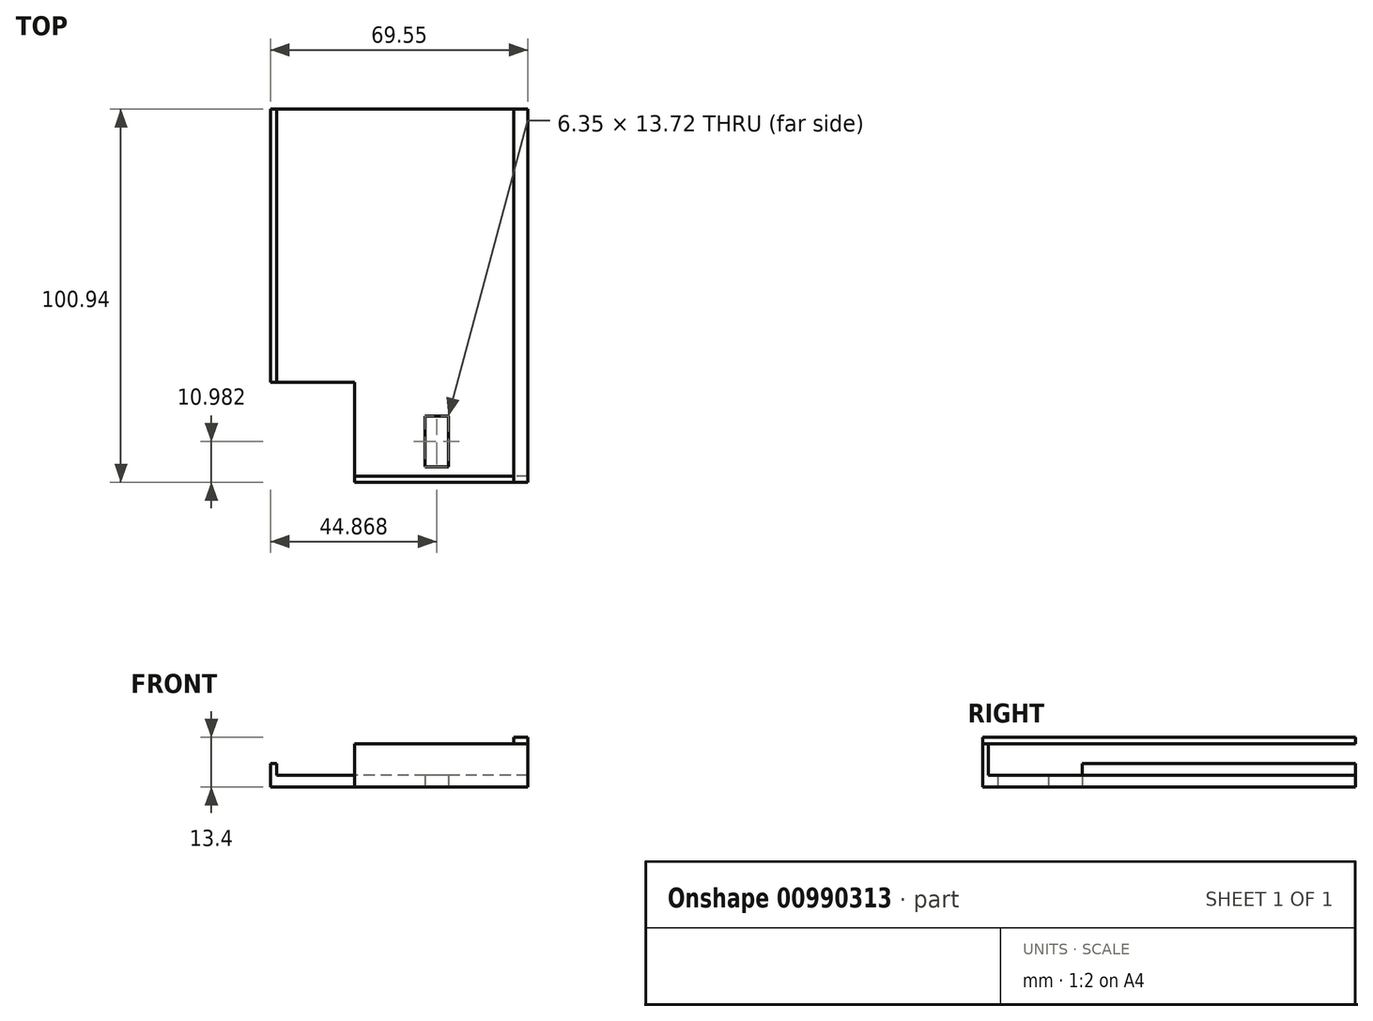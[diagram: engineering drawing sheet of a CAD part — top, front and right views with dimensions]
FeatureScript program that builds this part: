
annotation { "Feature Type Name" : "Feature", "Feature Type Description" : "" }
export const myFeature = defineFeature(function(context is Context, id is Id, definition is map)
    precondition{}
    {
        {
            var Q0;
            Q0=qCreatedBy(makeId("Top.planeOp"),FACE);
            var sketch = newSketch(context, id + "F0", { "sketchPlane" : qUnion([Q0])});
            skLineSegment(sketch, "E0.bottom", {"start": v(33.98, 49.68) * mm, "end": v(-33.98, 49.68) * mm});
            skLineSegment(sketch, "E0.top", {"start": v(33.98, -49.68) * mm, "end": v(-33.98, -49.68) * mm});
            skLineSegment(sketch, "E0.left", {"start": v(33.98, 49.68) * mm, "end": v(33.98, -49.68) * mm});
            skLineSegment(sketch, "E0.right", {"start": v(-33.98, 49.68) * mm, "end": v(-33.98, -49.68) * mm});
            skPoint(sketch, "E0.middle", {"position": v(0, 0) * mm});
            skLineSegment(sketch, "E1.bottom", {"start": v(33.98, 49.68) * mm, "end": v(33.98, 49.68) * mm});
            skLineSegment(sketch, "E1.top", {"start": v(33.98, -49.68) * mm, "end": v(33.98, -49.68) * mm});
            skLineSegment(sketch, "E2.top", {"start": v(-33.98, -24.28) * mm, "end": v(-12.93, -24.28) * mm});
            skLineSegment(sketch, "E2.right", {"start": v(-12.93, -49.68) * mm, "end": v(-12.93, -24.28) * mm});
            skLineSegment(sketch, "E3.bottom", {"start": v(-12.93, -49.68) * mm, "end": v(33.98, -49.68) * mm});
            skLineSegment(sketch, "E3.top", {"start": v(-12.93, -51.26) * mm, "end": v(33.98, -51.26) * mm});
            skLineSegment(sketch, "E3.left", {"start": v(-12.93, -49.68) * mm, "end": v(-12.93, -51.26) * mm});
            skLineSegment(sketch, "E3.right", {"start": v(33.98, -49.68) * mm, "end": v(33.98, -51.26) * mm});
            skLineSegment(sketch, "E4.bottom", {"start": v(-33.98, 49.68) * mm, "end": v(-35.57, 49.68) * mm});
            skLineSegment(sketch, "E4.top", {"start": v(-33.98, -49.68) * mm, "end": v(-35.57, -49.68) * mm});
            skLineSegment(sketch, "E4.right", {"start": v(-35.57, 49.68) * mm, "end": v(-35.57, -49.68) * mm});
            skLineSegment(sketch, "E5", {"start": v(-33.98, -43.18) * mm, "end": v(33.98, -43.18) * mm, "construction": true});
            skLineSegment(sketch, "E6", {"start": v(-33.98, -24.28) * mm, "end": v(-35.57, -24.28) * mm});
            skLineSegment(sketch, "E7.bottom", {"start": v(12.47, -47.14) * mm, "end": v(6.12, -47.14) * mm});
            skLineSegment(sketch, "E7.top", {"start": v(12.47, -33.42) * mm, "end": v(6.12, -33.42) * mm});
            skLineSegment(sketch, "E7.left", {"start": v(12.47, -47.14) * mm, "end": v(12.47, -33.42) * mm});
            skLineSegment(sketch, "E7.right", {"start": v(6.12, -47.14) * mm, "end": v(6.12, -33.42) * mm});
            skSolve(sketch);
        }
        {
            var Q0;
            {var subQ3=sQuery(id+"F0.wireOp",EDGE,"E0.bottom");Q0=makeQuery(id+"F0.imprint","IMPRINT",FACE,{"disambiguationData":[TD([[makeQuery(id+"F0.imprint","IMPRINT",EDGE,{"derivedFrom":subQ3}),1.0]])]});}
            extrude(context, id + "F1", {"entities" : qUnion([Q0]), "depth" : 3.17 * mm, "offsetDistance" : 25.4 * mm});
        }
        {
            var Q0;
            {var subQ3=sQuery(id+"F0.wireOp",EDGE,"E4.bottom");Q0=makeQuery(id+"F0.imprint","IMPRINT",FACE,{"disambiguationData":[TD([[makeQuery(id+"F0.imprint","IMPRINT",EDGE,{"derivedFrom":subQ3}),1.0]])]});}
            extrude(context, id + "F2", {"entities" : qUnion([Q0]), "operationType" : NewBodyOperationType.ADD, "depth" : 6.35 * mm, "offsetDistance" : 25.4 * mm});
        }
        {
            var Q0;
            Q0=makeQuery(id+"F0.imprint","IMPRINT",FACE,{"disambiguationData":[TD([[makeQuery(id+"F0.imprint","IMPRINT",EDGE,{"derivedFrom":sQuery(id+"F0.wireOp",EDGE,"E3.top")}),1.0]])]});
            var Q1;
            Q1=makeQuery(id+"F0.imprint","IMPRINT",FACE,{"disambiguationData":[TD([[makeQuery(id+"F0.imprint","IMPRINT",EDGE,{"derivedFrom":sQuery(id+"F0.wireOp",EDGE,"E1.bottom")}),-1.0]])]});
            extrude(context, id + "F3", {"entities" : qUnion([Q0, Q1]), "operationType" : NewBodyOperationType.ADD, "depth" : 11.68 * mm, "offsetDistance" : 25.4 * mm});
        }
        {
            var Q0;
            Q0=makeQuery(id+"F3.boolean.opBoolean","MERGE",FACE,{"derivedFrom":[makeQuery(id+"F2.boolean.opBoolean","MERGE",FACE,{"derivedFrom":[makeQuery(id+"F1.opExtrude","SWEPT_FACE",FACE,{"disambiguationData":[OSD([sQuery(id+"F0.wireOp",EDGE,"E0.bottom")])]}),makeQuery(id+"F2.opExtrude","SWEPT_FACE",FACE,{"disambiguationData":[OSD([sQuery(id+"F0.wireOp",EDGE,"E4.bottom")])]})]}),makeQuery(id+"F3.opExtrude","SWEPT_FACE",FACE,{"disambiguationData":[OSD([sQuery(id+"F0.wireOp",EDGE,"E1.bottom")])]})]});
            var sketch = newSketch(context, id + "F4", { "sketchPlane" : qUnion([Q0])});
            skLineSegment(sketch, "E8", {"start": v(-29.87, 11.68) * mm, "end": v(-42.97, 0) * mm});
            skSolve(sketch);
        }
        {
            var Q0;
            Q0=makeQuery(id+"F3.boolean.opBoolean","MERGE",FACE,{"derivedFrom":[makeQuery(id+"F1.opExtrude","SWEPT_FACE",FACE,{"disambiguationData":[OSD([sQuery(id+"F0.wireOp",EDGE,"E0.left")])]}),makeQuery(id+"F3.opExtrude","SWEPT_FACE",FACE,{"disambiguationData":[OSD([sQuery(id+"F0.wireOp",EDGE,"E3.right")])]})]});
            var sketch = newSketch(context, id + "F5", { "sketchPlane" : qUnion([Q0])});
            skLineSegment(sketch, "E9.bottom", {"start": v(-51.26, 11.68) * mm, "end": v(49.68, 11.68) * mm});
            skLineSegment(sketch, "E9.top", {"start": v(-51.26, 13.4) * mm, "end": v(49.68, 13.4) * mm});
            skLineSegment(sketch, "E9.left", {"start": v(-51.26, 11.68) * mm, "end": v(-51.26, 13.4) * mm});
            skLineSegment(sketch, "E9.right", {"start": v(49.68, 11.68) * mm, "end": v(49.68, 13.4) * mm});
            skSolve(sketch);
        }
        {
            var Q0;
            Q0=makeQuery(id+"F5.imprint","IMPRINT",FACE,{"disambiguationData":[TD([[makeQuery(id+"F5.imprint","IMPRINT",EDGE,{"derivedFrom":sQuery(id+"F5.wireOp",EDGE,"E9.top")}),-1.0]])]});
            extrude(context, id + "F6", {"entities" : qUnion([Q0]), "oppositeDirection" : true, "depth" : 3.8 * mm, "offsetDistance" : 25.4 * mm});
        }
    });
